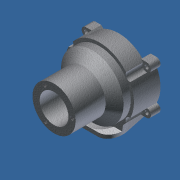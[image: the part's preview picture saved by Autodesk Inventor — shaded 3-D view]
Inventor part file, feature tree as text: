
AUTODESK INVENTOR PART (.ipt)
format: ipt  version: 2012 (Build 160160000, 160)  size: 323,072 bytes
history: native  units: in
note: dims shown in document units (in); Inventor stores cm internally (conversion verified against a paired STEP export)
features: extrude x10, projected_geometry x7, sketch x6, thread x3, revolve x1, plane x1, fillet x1
ambient origin geometry x8: Origin, YZ Plane, XZ Plane, XY Plane, X Axis, Y Axis, Z Axis, Center Point
bodies: Solid1 (feature_tree)
feature tree (29):
  extrude  "Extrusion1"  Depth=1.25in
  thread  "Thread1"  [1 undecoded]
  thread  "Thread2"  [1 undecoded]
  thread  "Thread3"  [1 undecoded]
  revolve  "Revolution1"  [1 undecoded]
  sketch  "Sketch4"  dims[d11=1.0in d12=0.0in d13=1.0in d14=0.0in]
  extrude  "Extrusion2"  Depth=1.0in TaperAngle=0.0deg
  extrude  "Extrusion3"  Depth=1.5in
  extrude  "Extrusion4"  Depth=0.25in
  extrude  "Extrusion5"  Depth=1.2in
  extrude  "Extrusion6"  Depth=0.6in
  extrude  "Extrusion7"  Depth=2.5in
  extrude  "Extrusion8"  TaperAngle=90.0deg  [1 undecoded]
  plane  "Work Plane1"
  sketch  "Sketch8"  dims[d20=0.0625in d21=1.2in d23=0.6in d24=2.5in d25=90.0deg d26=2.518in d27=0.3in d28=0.134in d29=0.6875in d30=0.3in d31=0.134in d32=0.3in d33=0.134in d34=0.3in d35=0.134in d36=2.4in d37=2.064in d38=0.0575in d39=0.335in d40=0.0in d41=0.335in d42=0.0in d43=1.0in d44=0.0in d45=0.75in d46=0.0in d47=0.25in d48=0.0in d49=1.0in d50=0.0in d52=1.5375in d53=0.7688in d54=1.25in d55=0.0in d57=1.0in d58=0.0625in d59=1.25in d60=0.0in d61=1.25in d62=0.0in d63=0.5in d64=0.5in d66=1.0547in]
  extrude  "Extrusion9"  Depth=2.518in
  extrude  "Extrusion10"  Depth=0.3in
  fillet  "Fillet1"  Radius=0.134in
  sketch  "Sketch1"  dims[d0=1.5in d1=1.25in d2=0.325in d3=0.128in d4=1.1811in d6=360.0deg]
  sketch  "Sketch3"  dims[d8=1.0in d9=0.98in d10=0.0in]
  projected_geometry  "Projected Loop1"
  sketch  "Sketch5"  dims[d15=1.0in d16=0.0in d17=1.5in]
  projected_geometry  "Projected Loop2"
  projected_geometry  "Projected Loop3"
  projected_geometry  "Projected Loop4"
  projected_geometry  "Projected Loop5"
  sketch  "Sketch6"  dims[d18=1.0875in d19=0.25in]
  projected_geometry  "Projected Loop7"
  projected_geometry  "Projected Loop8"
note: 5 required parameter values undecoded (feature->parameter linkage not recoverable at this tier; creation-order binding heuristic only, values carry confidence <= 0.55)